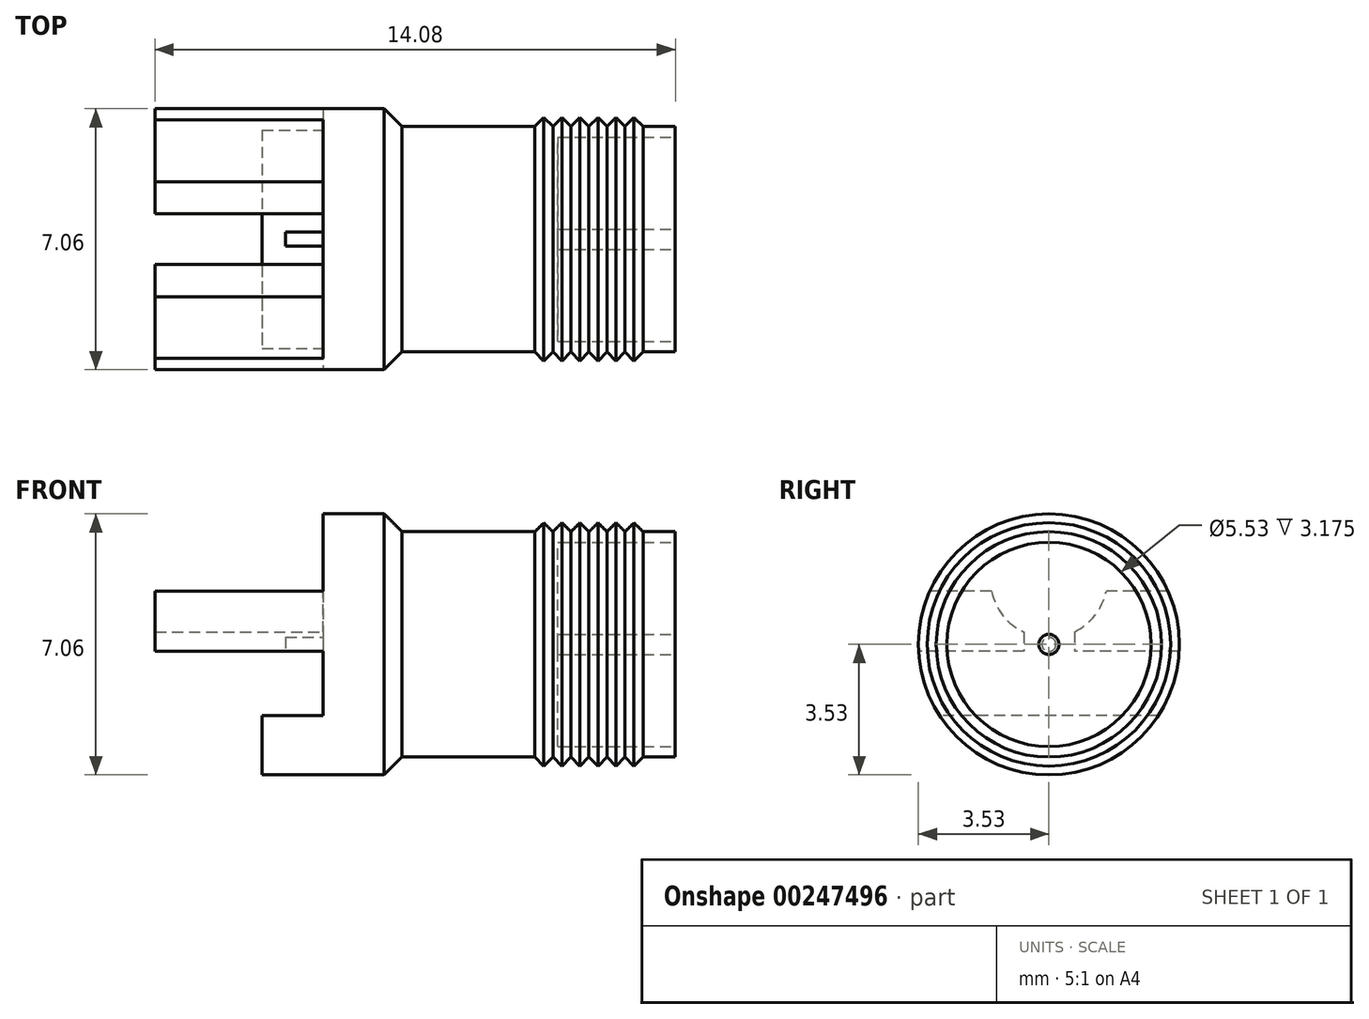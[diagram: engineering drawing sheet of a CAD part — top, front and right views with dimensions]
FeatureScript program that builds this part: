
annotation { "Feature Type Name" : "Feature", "Feature Type Description" : "" }
export const myFeature = defineFeature(function(context is Context, id is Id, definition is map)
    precondition{}
    {
        {
            var Q0;
            Q0=qCreatedBy(makeId("Front.planeOp"),FACE);
            var sketch = newSketch(context, id + "F0", { "sketchPlane" : qUnion([Q0])});
            skLineSegment(sketch, "E0", {"start": v(0, 0) * mm, "end": v(9.52, 0) * mm});
            skLineSegment(sketch, "E1", {"start": v(9.53, 0) * mm, "end": v(9.53, 3.05) * mm});
            skLineSegment(sketch, "E2", {"start": v(7.68, 3.05) * mm, "end": v(7.44, 3.3) * mm});
            skLineSegment(sketch, "E3", {"start": v(7.44, 3.3) * mm, "end": v(7.2, 3.05) * mm});
            skLineSegment(sketch, "E4", {"start": v(7.2, 3.05) * mm, "end": v(6.95, 3.3) * mm});
            skLineSegment(sketch, "E5", {"start": v(6.95, 3.3) * mm, "end": v(6.7, 3.05) * mm});
            skLineSegment(sketch, "E6", {"start": v(6.7, 3.05) * mm, "end": v(6.46, 3.3) * mm});
            skLineSegment(sketch, "E7", {"start": v(6.46, 3.3) * mm, "end": v(6.22, 3.05) * mm});
            skLineSegment(sketch, "E8", {"start": v(6.22, 3.05) * mm, "end": v(5.97, 3.3) * mm});
            skLineSegment(sketch, "E9", {"start": v(5.97, 3.3) * mm, "end": v(5.73, 3.05) * mm});
            skLineSegment(sketch, "E10", {"start": v(5.73, 3.05) * mm, "end": v(2.13, 3.05) * mm});
            skLineSegment(sketch, "E11", {"start": v(2.13, 3.05) * mm, "end": v(1.65, 3.53) * mm});
            skLineSegment(sketch, "E12", {"start": v(1.65, 3.53) * mm, "end": v(0, 3.53) * mm});
            skLineSegment(sketch, "E13", {"start": v(0, 3.53) * mm, "end": v(0, 0) * mm});
            skLineSegment(sketch, "E14", {"start": v(7.68, 3.05) * mm, "end": v(7.92, 3.3) * mm});
            skLineSegment(sketch, "E15", {"start": v(7.92, 3.3) * mm, "end": v(8.17, 3.05) * mm});
            skLineSegment(sketch, "E16", {"start": v(8.17, 3.05) * mm, "end": v(8.41, 3.3) * mm});
            skLineSegment(sketch, "E17", {"start": v(8.41, 3.3) * mm, "end": v(8.65, 3.05) * mm});
            skLineSegment(sketch, "E18", {"start": v(8.65, 3.05) * mm, "end": v(9.53, 3.05) * mm});
            skSolve(sketch);
        }
        {
            var Q0;
            Q0=qSketchRegion(id+"F0",true);
            var Q1;
            Q1=sQuery(id+"F0.wireOp",EDGE,"E0");
            revolve(context, id + "F1", {"entities" : qUnion([Q0]), "axis" : qUnion([Q1]), "revolveType" : RevolveType.FULL});
        }
        {
            var Q0;
            Q0=makeQuery(id+"F1.opRevolve","SWEPT_FACE",FACE,{"disambiguationData":[OSD([sQuery(id+"F0.wireOp",EDGE,"E1")])]});
            var sketch = newSketch(context, id + "F2", { "sketchPlane" : qUnion([Q0])});
            skCircle(sketch, "E19", {"center": v(0, 0) * mm, "radius": 0.27 * mm});
            skCircle(sketch, "E20", {"center": v(0, 0) * mm, "radius": 2.76 * mm});
            skSolve(sketch);
        }
        {
            var Q0;
            Q0=qSketchRegion(id+"F2",true);
            extrude(context, id + "F3", {"entities" : qUnion([Q0]), "operationType" : NewBodyOperationType.REMOVE, "oppositeDirection" : true, "depth" : 3.17 * mm});
        }
        {
            var Q0;
            Q0=makeQuery(id+"F1.opRevolve","SWEPT_FACE",FACE,{"disambiguationData":[OSD([sQuery(id+"F0.wireOp",EDGE,"E13")])]});
            var sketch = newSketch(context, id + "F4", { "sketchPlane" : qUnion([Q0])});
            skCircle(sketch, "E21", {"center": v(0, 0) * mm, "radius": 0.2 * mm});
            skSolve(sketch);
        }
        {
            var Q0;
            Q0=qSketchRegion(id+"F4",true);
            extrude(context, id + "F5", {"entities" : qUnion([Q0]), "operationType" : NewBodyOperationType.ADD, "depth" : 1.02 * mm});
        }
        {
            var Q0;
            Q0=makeQuery(id+"F1.opRevolve","SWEPT_FACE",FACE,{"disambiguationData":[OSD([sQuery(id+"F0.wireOp",EDGE,"E13")])]});
            var sketch = newSketch(context, id + "F6", { "sketchPlane" : qUnion([Q0])});
            skArc(sketch, "E22", {"start": v(2.96, -1.93) * mm, "mid": v(0, -3.53) * mm, "end": v(-2.96, -1.93) * mm});
            skLineSegment(sketch, "E23", {"start": v(-2.96, -1.93) * mm, "end": v(2.96, -1.93) * mm});
            skSolve(sketch);
        }
        {
            var Q0;
            Q0=qSketchRegion(id+"F6",true);
            extrude(context, id + "F7", {"entities" : qUnion([Q0]), "operationType" : NewBodyOperationType.ADD, "depth" : 1.65 * mm});
        }
        {
            var Q0;
            Q0=makeQuery(id+"F1.opRevolve","SWEPT_FACE",FACE,{"disambiguationData":[OSD([sQuery(id+"F0.wireOp",EDGE,"E13")])]});
            var sketch = newSketch(context, id + "F8", { "sketchPlane" : qUnion([Q0])});
            skArc(sketch, "E24", {"start": v(-3.23, 1.43) * mm, "mid": v(0, -3.53) * mm, "end": v(3.23, 1.43) * mm});
            skLineSegment(sketch, "E25", {"start": v(-3.53, -0.2) * mm, "end": v(-0.7, -0.2) * mm});
            skLineSegment(sketch, "E26", {"start": v(-3.23, 1.43) * mm, "end": v(-1.55, 1.43) * mm});
            skLineSegment(sketch, "E27", {"start": v(0, 0) * mm, "end": v(0, 5.47) * mm, "construction": true});
            skPoint(sketch, "E27.endSnap0", {"position": v(0, 3.53) * mm});
            skArc(sketch, "E28", {"start": v(-1.55, 1.43) * mm, "mid": v(-1.25, 0.79) * mm, "end": v(-0.7, 0.34) * mm});
            skLineSegment(sketch, "E29", {"start": v(-0.7, 0.34) * mm, "end": v(-0.7, -0.2) * mm});
            skLineSegment(sketch, "E30", {"start": v(0.68, 0.33) * mm, "end": v(0.68, -0.2) * mm});
            skArc(sketch, "E31.trimOffspring", {"start": v(0.68, 0.33) * mm, "mid": v(1.24, 0.78) * mm, "end": v(1.55, 1.43) * mm});
            skLineSegment(sketch, "E32.trimOffspring", {"start": v(0.68, -0.2) * mm, "end": v(3.53, -0.2) * mm});
            skLineSegment(sketch, "E33.trimOffspring", {"start": v(1.55, 1.43) * mm, "end": v(3.23, 1.43) * mm});
            skSolve(sketch);
        }
        {
            var Q0;
            Q0=qSketchRegion(id+"F8",true);
            extrude(context, id + "F9", {"entities" : qUnion([Q0]), "operationType" : NewBodyOperationType.ADD, "depth" : 4.55 * mm});
        }
    });
